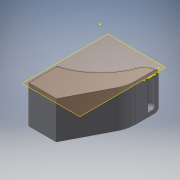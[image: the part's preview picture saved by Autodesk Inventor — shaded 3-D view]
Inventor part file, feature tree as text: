
AUTODESK INVENTOR PART (.ipt)
format: ipt  version: 2016 (Build 200138000, 138)  size: 229,376 bytes
history: native  units: mm
features: sketch x6, fillet x5, reference x5, extrude x3, plane x1, chamfer x1, shell x1, projected_geometry x1
ambient origin geometry x8: Origin, YZ Plane, XZ Plane, XY Plane, X Axis, Y Axis, Z Axis, Center Point
bodies: Solid1 (feature_tree)
feature tree (23):
  plane  "Work Plane1"
  extrude  "Extrusion1"  Depth=25.0mm TaperAngle=45.0deg
  chamfer  "Chamfer1"  Distance=2.0mm
  sketch  "Sketch2"  dims[d5=2.0mm]
  shell  "Shell1"  Thickness=3.0mm
  extrude  "Extrusion2"  Depth=2.0mm
  sketch  "Sketch4"  dims[d10=5.5mm d11=2.0mm d12=17.25mm d13=4.0mm d14=16.0mm d15=0.0mm]
  sketch  "Sketch5"
  fillet  "Fillet1"  Radius=17.25mm
  fillet  "Fillet2"  Radius=4.0mm
  fillet  "Fillet3"  Radius=16.0mm
  fillet  "Fillet4"  [1 undecoded]
  fillet  "Fillet5"  [1 undecoded]
  extrude  "Extrusion3"  [1 undecoded]
  sketch  "Sketch1"  dims[d0=20.0mm d1=0.0mm d2=25.0mm d3=13.0mm d4=45.0deg]
  sketch  "Sketch3"  dims[d6=8.0mm d7=2.0mm d8=0.0mm d9=3.0mm]
  reference  "Reference1"
  projected_geometry  "Projected Loop1"
  sketch  "Sketch6"
  reference  "Reference2"
  reference  "Reference3"
  reference  "Reference4"
  reference  "Reference5"
note: 3 required parameter values undecoded (feature->parameter linkage not recoverable at this tier; creation-order binding heuristic only, values carry confidence <= 0.55)
